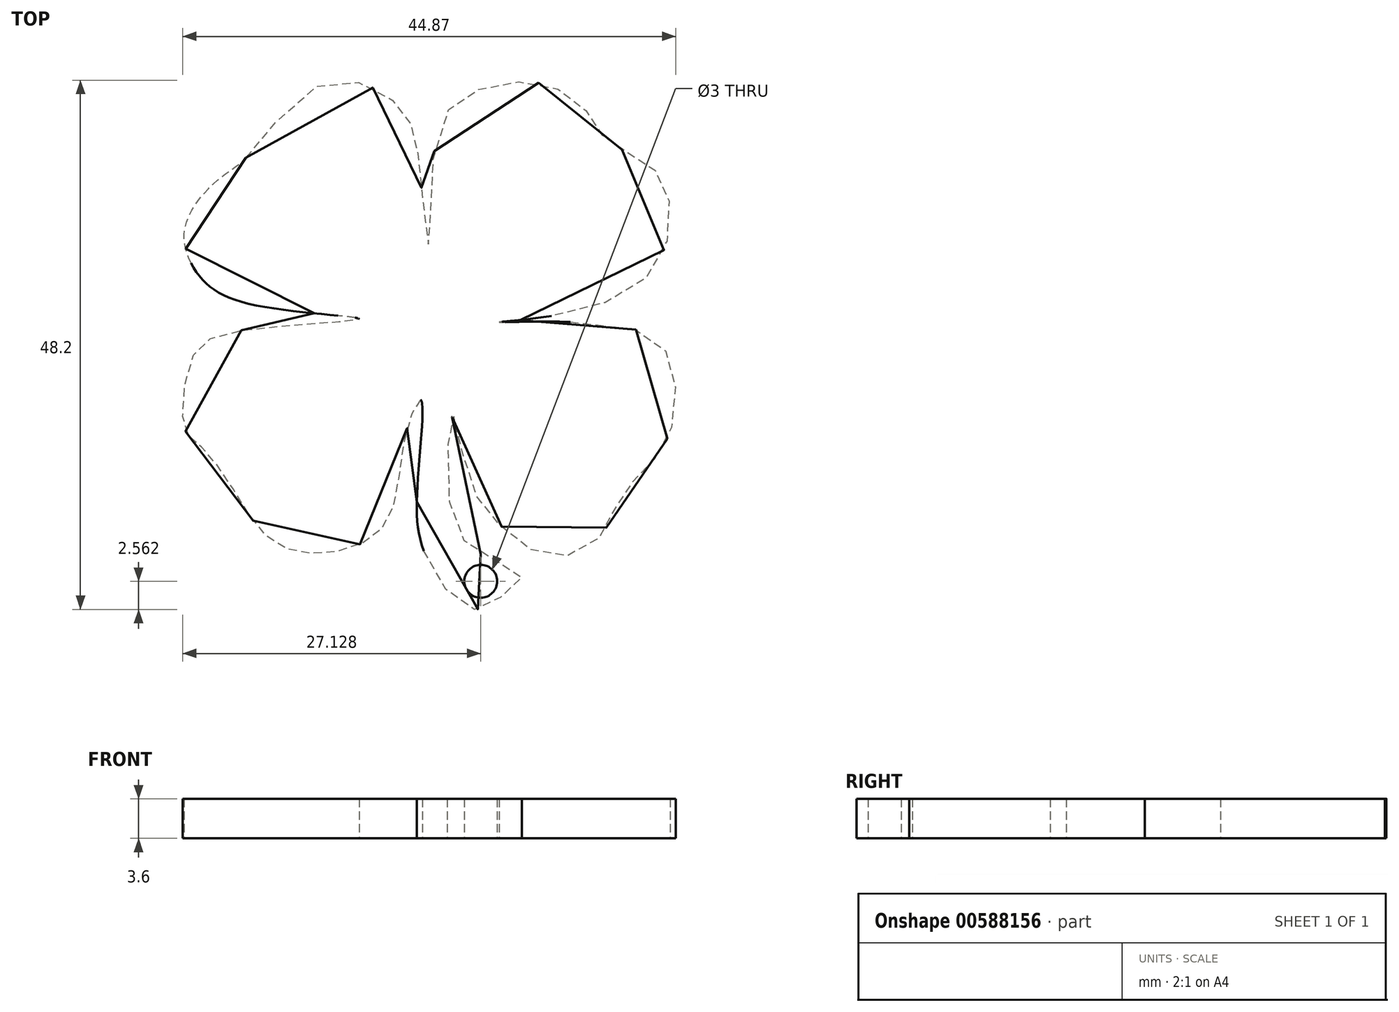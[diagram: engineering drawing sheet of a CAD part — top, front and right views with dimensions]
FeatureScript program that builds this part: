
annotation { "Feature Type Name" : "Feature", "Feature Type Description" : "" }
export const myFeature = defineFeature(function(context is Context, id is Id, definition is map)
    precondition{}
    {
        {
            var Q0;
            Q0=qCreatedBy(makeId("Top.planeOp"),FACE);
            var sketch = newSketch(context, id + "F0", { "sketchPlane" : qUnion([Q0])});
            skFitSpline(sketch, "E0", {"points": [v(-30.68, 31.58) * mm, v(-23.9, 38.25) * mm, v(-17.99, 37.32) * mm, v(-15.65, 34.57) * mm, v(-14.83, 29.95) * mm, v(-14, 23.57) * mm, v(-13.25, 33.69) * mm, v(-9.56, 37.78) * mm, v(-3.36, 38.25) * mm, v(0.56, 35.5) * mm, v(2.25, 33.1) * mm, v(5.94, 31) * mm, v(7.87, 27.25) * mm, v(6.17, 21.11) * mm, v(-2.43, 17.25) * mm, v(-7.63, 16.6) * mm, v(3.95, 16.14) * mm, v(7.93, 13.04) * mm, v(8.1, 7.25) * mm, v(5.82, 3.39) * mm, v(3.36, 0.64) * mm, v(1.55, -2.93) * mm, v(-2.9, -4.74) * mm, v(-7.46, -2) * mm, v(-10.44, 2.57) * mm, v(-11.85, 8.07) * mm, v(-12.25, 0.82) * mm, v(-9.47, -4.41) * mm, v(-5.6, -6.46) * mm, v(-7.58, -8.49) * mm, v(-10.29, -9.49) * mm, v(-14.17, -5) * mm, v(-15.06, 1.98) * mm, v(-14.77, 9.53) * mm, v(-16.12, 6.6) * mm, v(-17.4, -0.53) * mm, v(-19.98, -3.46) * mm, v(-24.89, -4.45) * mm, v(-28.75, -2.93) * mm, v(-32.08, 1.8) * mm, v(-34.95, 5.44) * mm, v(-36.24, 6.84) * mm, v(-35.65, 13.16) * mm, v(-31.56, 15.79) * mm, v(-20.39, 16.9) * mm, v(-29.69, 18.13) * mm, v(-35, 20.94) * mm, v(-36.18, 25.44) * mm, v(-32.79, 29.95) * mm, v(-30.68, 31.58) * mm]});
            skCircle(sketch, "E1", {"center": v(-9.32, -6.99) * mm, "radius": 1.5 * mm});
            skSolve(sketch);
        }
        {
            var Q0;
            Q0 = qSketchRegion(id + "F0", true);
            extrude(context, id + "F1", {"entities" : qUnion([Q0]), "depth" : 3.6 * mm, "offsetDistance" : 25.4 * mm});
        }
    });
